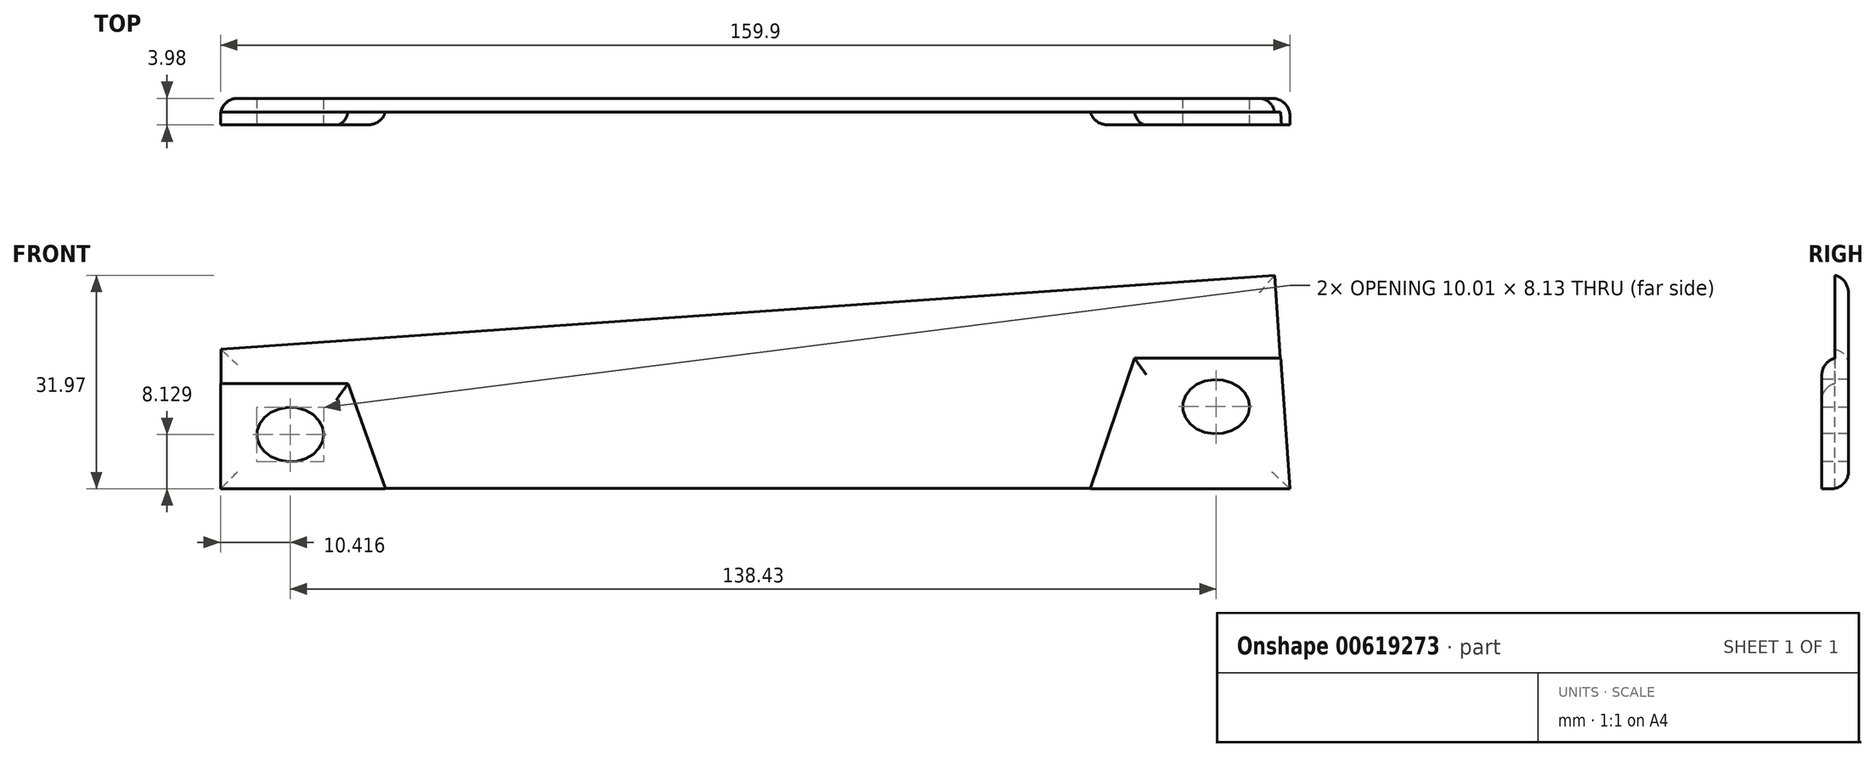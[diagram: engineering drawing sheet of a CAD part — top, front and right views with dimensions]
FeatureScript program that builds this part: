
annotation { "Feature Type Name" : "Feature", "Feature Type Description" : "" }
export const myFeature = defineFeature(function(context is Context, id is Id, definition is map)
    precondition{}
    {
        {
            var Q0;
            Q0=qCreatedBy(makeId("Front.planeOp"),FACE);
            var sketch = newSketch(context, id + "F0", { "sketchPlane" : qUnion([Q0])});
            skLineSegment(sketch, "E0", {"start": v(-60.54, 4.55) * mm, "end": v(-60.54, -18.3) * mm, "construction": true});
            skLineSegment(sketch, "E1", {"start": v(36.48, 11.38) * mm, "end": v(36.48, -18.3) * mm, "construction": true});
            skLineSegment(sketch, "E2", {"start": v(-130, -18.3) * mm, "end": v(154.95, -18.3) * mm, "construction": true});
            skLineSegment(sketch, "E3", {"start": v(-139.87, -1.03) * mm, "end": v(162.35, 20.25) * mm, "construction": true});
            skPoint(sketch, "E4", {"position": v(-78.37, -10.18) * mm});
            skPoint(sketch, "E5", {"position": v(60.06, -6.02) * mm});
            skEllipse(sketch, "E6", {"center": v(-78.37, -10.18) * mm, "majorRadius": 5 * mm, "minorRadius": 4.06 * mm, "majorAxis": v(1, 0)});
            skEllipse(sketch, "E7", {"center": v(60.06, -6.02) * mm, "majorRadius": 5 * mm, "minorRadius": 4.06 * mm, "majorAxis": v(1, 0)});
            skLineSegment(sketch, "E8", {"start": v(-88.79, 2.56) * mm, "end": v(-88.79, -18.3) * mm});
            skLineSegment(sketch, "E9", {"start": v(-88.79, -18.3) * mm, "end": v(71.1, -18.3) * mm});
            skLineSegment(sketch, "E10", {"start": v(71.1, -18.3) * mm, "end": v(68.85, 13.66) * mm});
            skLineSegment(sketch, "E11", {"start": v(68.85, 13.66) * mm, "end": v(-88.79, 2.56) * mm});
            skSolve(sketch);
        }
        {
            var Q0;
            Q0=makeQuery(id+"F0.imprint","IMPRINT",FACE,{"disambiguationData":[TD([[makeQuery(id+"F0.imprint","IMPRINT",EDGE,{"derivedFrom":sQuery(id+"F0.wireOp",EDGE,"E6")}),-1.0]])]});
            extrude(context, id + "F1", {"entities" : qUnion([Q0]), "depth" : 2.03 * mm, "offsetDistance" : 25.4 * mm});
        }
        {
            var Q0;
            Q0=makeQuery(id+"F1.opExtrude","CAP_FACE",FACE,{"disambiguationData":[OSD([sQuery(id+"F0.wireOp",EDGE,"E6"),sQuery(id+"F0.wireOp",EDGE,"E7"),sQuery(id+"F0.wireOp",EDGE,"E8"),sQuery(id+"F0.wireOp",EDGE,"E9"),sQuery(id+"F0.wireOp",EDGE,"E10"),sQuery(id+"F0.wireOp",EDGE,"E11")])],"isStart":false});
            var sketch = newSketch(context, id + "F2", { "sketchPlane" : qUnion([Q0])});
            skLineSegment(sketch, "E12", {"start": v(41.26, -18.3) * mm, "end": v(47.86, 1.22) * mm});
            skLineSegment(sketch, "E13", {"start": v(47.86, 1.22) * mm, "end": v(69.73, 1.22) * mm});
            skEllipse(sketch, "E14.0", {"center": v(60.06, -6.02) * mm, "majorRadius": 5 * mm, "minorRadius": 4.06 * mm, "majorAxis": v(1, 0)});
            skLineSegment(sketch, "E15.0", {"start": v(-88.79, -18.3) * mm, "end": v(-64.15, -18.3) * mm});
            skLineSegment(sketch, "E16.0", {"start": v(71.1, -18.3) * mm, "end": v(69.73, 1.22) * mm});
            skLineSegment(sketch, "E17.0", {"start": v(-88.79, -2.56) * mm, "end": v(-88.79, -18.3) * mm});
            skEllipse(sketch, "E18.0", {"center": v(-78.37, -10.18) * mm, "majorRadius": 5 * mm, "minorRadius": 4.06 * mm, "majorAxis": v(1, 0)});
            skLineSegment(sketch, "E19", {"start": v(-64.15, -18.3) * mm, "end": v(-69.74, -2.56) * mm});
            skLineSegment(sketch, "E20", {"start": v(-69.74, -2.56) * mm, "end": v(-88.79, -2.56) * mm});
            skPoint(sketch, "E21.orphan", {"position": v(-88.79, 2.56) * mm});
            skLineSegment(sketch, "E22.trimOffspring", {"start": v(41.26, -18.3) * mm, "end": v(71.1, -18.3) * mm});
            skPoint(sketch, "E23.orphan", {"position": v(68.85, 13.66) * mm});
            skSolve(sketch);
        }
        {
            var Q0;
            Q0=makeQuery(id+"F2.imprint","IMPRINT",FACE,{"disambiguationData":[TD([[makeQuery(id+"F2.imprint","IMPRINT",EDGE,{"derivedFrom":sQuery(id+"F2.wireOp",EDGE,"E15.0")}),1.0]])]});
            var Q1;
            Q1=makeQuery(id+"F2.imprint","IMPRINT",FACE,{"disambiguationData":[TD([[makeQuery(id+"F2.imprint","IMPRINT",EDGE,{"derivedFrom":sQuery(id+"F2.wireOp",EDGE,"E12")}),-1.0]])]});
            extrude(context, id + "F3", {"entities" : qUnion([Q0, Q1]), "operationType" : NewBodyOperationType.ADD, "depth" : 1.94 * mm, "offsetDistance" : 25.4 * mm});
        }
        {
            var Q0;
            Q0=makeQuery(id+"F3.opExtrude","CAP_EDGE",EDGE,{"disambiguationData":[OSD([sQuery(id+"F2.wireOp",EDGE,"E13")])],"isStart":false});
            var Q1;
            Q1=makeQuery(id+"F3.opExtrude","CAP_EDGE",EDGE,{"disambiguationData":[OSD([sQuery(id+"F2.wireOp",EDGE,"E12")])],"isStart":false});
            var Q2;
            Q2=makeQuery(id+"F3.opExtrude","CAP_EDGE",EDGE,{"disambiguationData":[OSD([sQuery(id+"F2.wireOp",EDGE,"E20")])],"isStart":false});
            var Q3;
            Q3=makeQuery(id+"F3.opExtrude","CAP_EDGE",EDGE,{"disambiguationData":[OSD([sQuery(id+"F2.wireOp",EDGE,"E19")])],"isStart":false});
            fillet(context, id + "F4", {"entities" : qUnion([Q0, Q1, Q2, Q3]), "radius" : 2.54 * mm, "tangentPropagation" : true, "allowEdgeOverflow" : false});
        }
        {
            var Q0;
            Q0=makeQuery(id+"F1.opExtrude","CAP_EDGE",EDGE,{"disambiguationData":[OSD([sQuery(id+"F0.wireOp",EDGE,"E11")])],"isStart":true});
            var Q1;
            Q1=makeQuery(id+"F1.opExtrude","CAP_EDGE",EDGE,{"disambiguationData":[OSD([sQuery(id+"F0.wireOp",EDGE,"E10")])],"isStart":true});
            var Q2;
            Q2=makeQuery(id+"F1.opExtrude","CAP_EDGE",EDGE,{"disambiguationData":[OSD([sQuery(id+"F0.wireOp",EDGE,"E9")])],"isStart":true});
            var Q3;
            Q3=makeQuery(id+"F1.opExtrude","CAP_EDGE",EDGE,{"disambiguationData":[OSD([sQuery(id+"F0.wireOp",EDGE,"E8")])],"isStart":true});
            fillet(context, id + "F5", {"entities" : qUnion([Q0, Q1, Q2, Q3]), "radius" : 2.54 * mm, "tangentPropagation" : true, "allowEdgeOverflow" : false});
        }
    });
